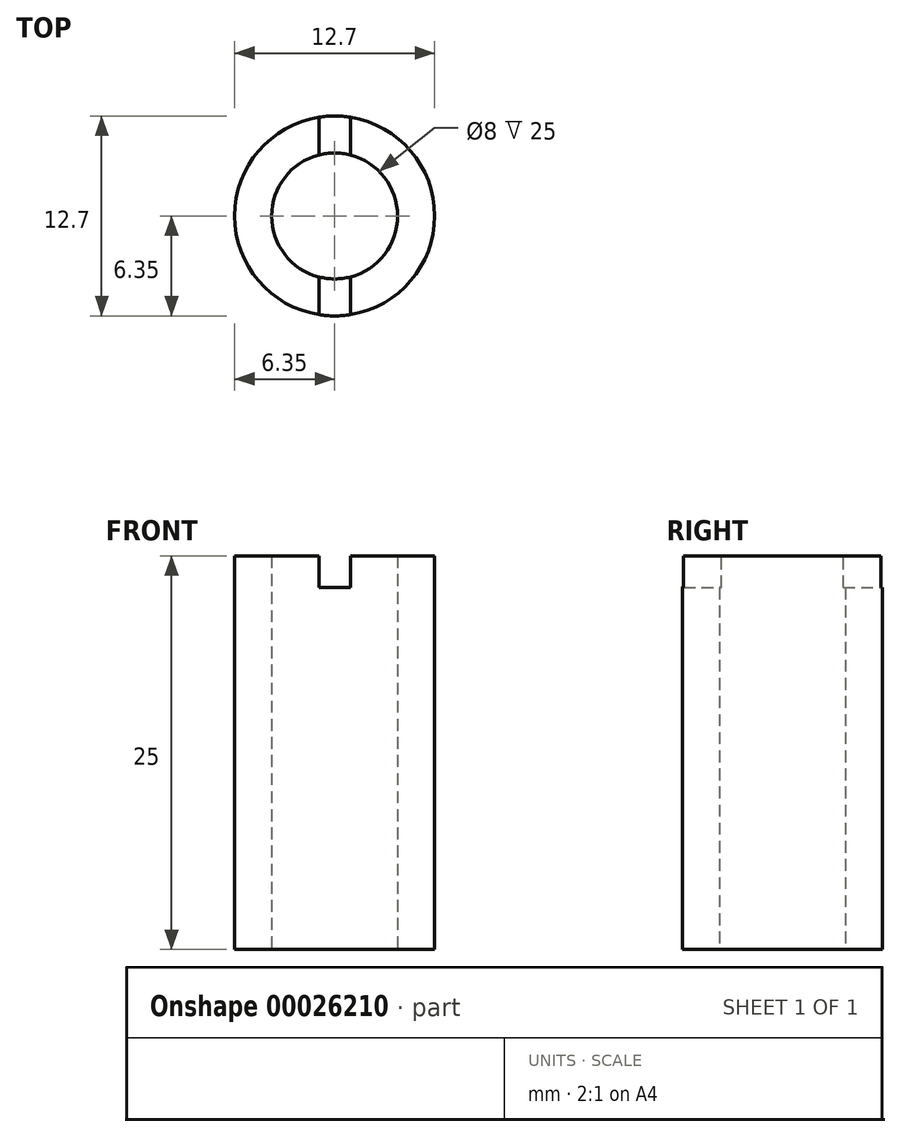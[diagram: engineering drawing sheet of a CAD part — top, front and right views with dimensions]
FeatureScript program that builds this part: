
annotation { "Feature Type Name" : "Feature", "Feature Type Description" : "" }
export const myFeature = defineFeature(function(context is Context, id is Id, definition is map)
    precondition{}
    {
        {
            var Q0;
            Q0=qCreatedBy(makeId("Top.planeOp"),FACE);
            var sketch = newSketch(context, id + "F0", { "sketchPlane" : qUnion([Q0])});
            skCircle(sketch, "E0", {"center": v(0, 0) * mm, "radius": 6.35 * mm});
            skCircle(sketch, "E1", {"center": v(0, 0) * mm, "radius": 4 * mm});
            skSolve(sketch);
        }
        {
            var Q0;
            Q0 = qSketchRegion(id + "F0", true);
            var Q1;
            Q1=makeQuery(id+"F0.imprint","IMPRINT",FACE,{"disambiguationData":[TD([[makeQuery(id+"F0.imprint","IMPRINT",EDGE,{"derivedFrom":sQuery(id+"F0.wireOp",EDGE,"E0")}),1.0]])]});
            extrude(context, id + "F1", {"entities" : qUnion([Q0, Q1]), "depth" : 25 * mm});
        }
        {
            var Q0;
            Q0=makeQuery(id+"F1.opExtrude","CAP_FACE",FACE,{"disambiguationData":[OSD([sQuery(id+"F0.wireOp",EDGE,"E0"),sQuery(id+"F0.wireOp",EDGE,"E1")])],"isStart":false});
            var sketch = newSketch(context, id + "F2", { "sketchPlane" : qUnion([Q0])});
            skLineSegment(sketch, "E2", {"start": v(0, -6.35) * mm, "end": v(0, 6.35) * mm});
            skLineSegment(sketch, "E3.0", {"start": v(1, -6.35) * mm, "end": v(1, 6.35) * mm});
            skLineSegment(sketch, "E4.0", {"start": v(-1, -6.35) * mm, "end": v(-1, 6.35) * mm});
            skSolve(sketch);
        }
        {
            var Q0;
            {var subQ3=sQuery(id+"F2.wireOp",EDGE,"E2");var subQ5=makeQuery(id+"F1.opExtrude","CAP_EDGE",EDGE,{"disambiguationData":[OSD([sQuery(id+"F0.wireOp",EDGE,"E0")])],"isStart":false});var subQ7=makeQuery(id+"F2.imprint","INTERSECT",VERTEX,{"disambiguationData":[OD(0.0)],"derivedFrom":[subQ5,subQ3]});Q0=makeQuery(id+"F2.imprint","IMPRINT",FACE,{"disambiguationData":[TD([[makeQuery(id+"F2.imprint","IMPRINT",EDGE,{"disambiguationData":[TD([[subQ7,-1.0]])],"derivedFrom":subQ3}),-1.0]])]});}
            var Q1;
            {var subQ3=sQuery(id+"F2.wireOp",EDGE,"E2");var subQ5=makeQuery(id+"F1.opExtrude","CAP_EDGE",EDGE,{"disambiguationData":[OSD([sQuery(id+"F0.wireOp",EDGE,"E0")])],"isStart":false});var subQ7=makeQuery(id+"F2.imprint","INTERSECT",VERTEX,{"disambiguationData":[OD(0.0)],"derivedFrom":[subQ5,subQ3]});Q1=makeQuery(id+"F2.imprint","IMPRINT",FACE,{"disambiguationData":[TD([[makeQuery(id+"F2.imprint","IMPRINT",EDGE,{"disambiguationData":[TD([[subQ7,-1.0]])],"derivedFrom":subQ3}),1.0]])]});}
            var Q2;
            {var subQ3=sQuery(id+"F2.wireOp",EDGE,"E2");var subQ5=makeQuery(id+"F1.opExtrude","CAP_EDGE",EDGE,{"disambiguationData":[OSD([sQuery(id+"F0.wireOp",EDGE,"E0")])],"isStart":false});var subQ7=makeQuery(id+"F2.imprint","INTERSECT",VERTEX,{"disambiguationData":[OD(1.0)],"derivedFrom":[subQ5,subQ3]});Q2=makeQuery(id+"F2.imprint","IMPRINT",FACE,{"disambiguationData":[TD([[makeQuery(id+"F2.imprint","IMPRINT",EDGE,{"disambiguationData":[TD([[subQ7,1.0]])],"derivedFrom":subQ3}),-1.0]])]});}
            var Q3;
            {var subQ3=sQuery(id+"F2.wireOp",EDGE,"E2");var subQ5=makeQuery(id+"F1.opExtrude","CAP_EDGE",EDGE,{"disambiguationData":[OSD([sQuery(id+"F0.wireOp",EDGE,"E0")])],"isStart":false});var subQ7=makeQuery(id+"F2.imprint","INTERSECT",VERTEX,{"disambiguationData":[OD(1.0)],"derivedFrom":[subQ5,subQ3]});Q3=makeQuery(id+"F2.imprint","IMPRINT",FACE,{"disambiguationData":[TD([[makeQuery(id+"F2.imprint","IMPRINT",EDGE,{"disambiguationData":[TD([[subQ7,1.0]])],"derivedFrom":subQ3}),1.0]])]});}
            extrude(context, id + "F3", {"entities" : qUnion([Q0, Q1, Q2, Q3]), "operationType" : NewBodyOperationType.REMOVE, "oppositeDirection" : true, "depth" : 2 * mm});
        }
        {
            var Q0;
            Q0=qCreatedBy(makeId("Front.planeOp"),FACE);
            cPlane(context, id + "F4", {"entities" : qUnion([Q0]), "cplaneType" : CPlaneType.OFFSET, "offset" : 150 * mm, "width" : 150 * mm, "height" : 150 * mm});
        }
    });
